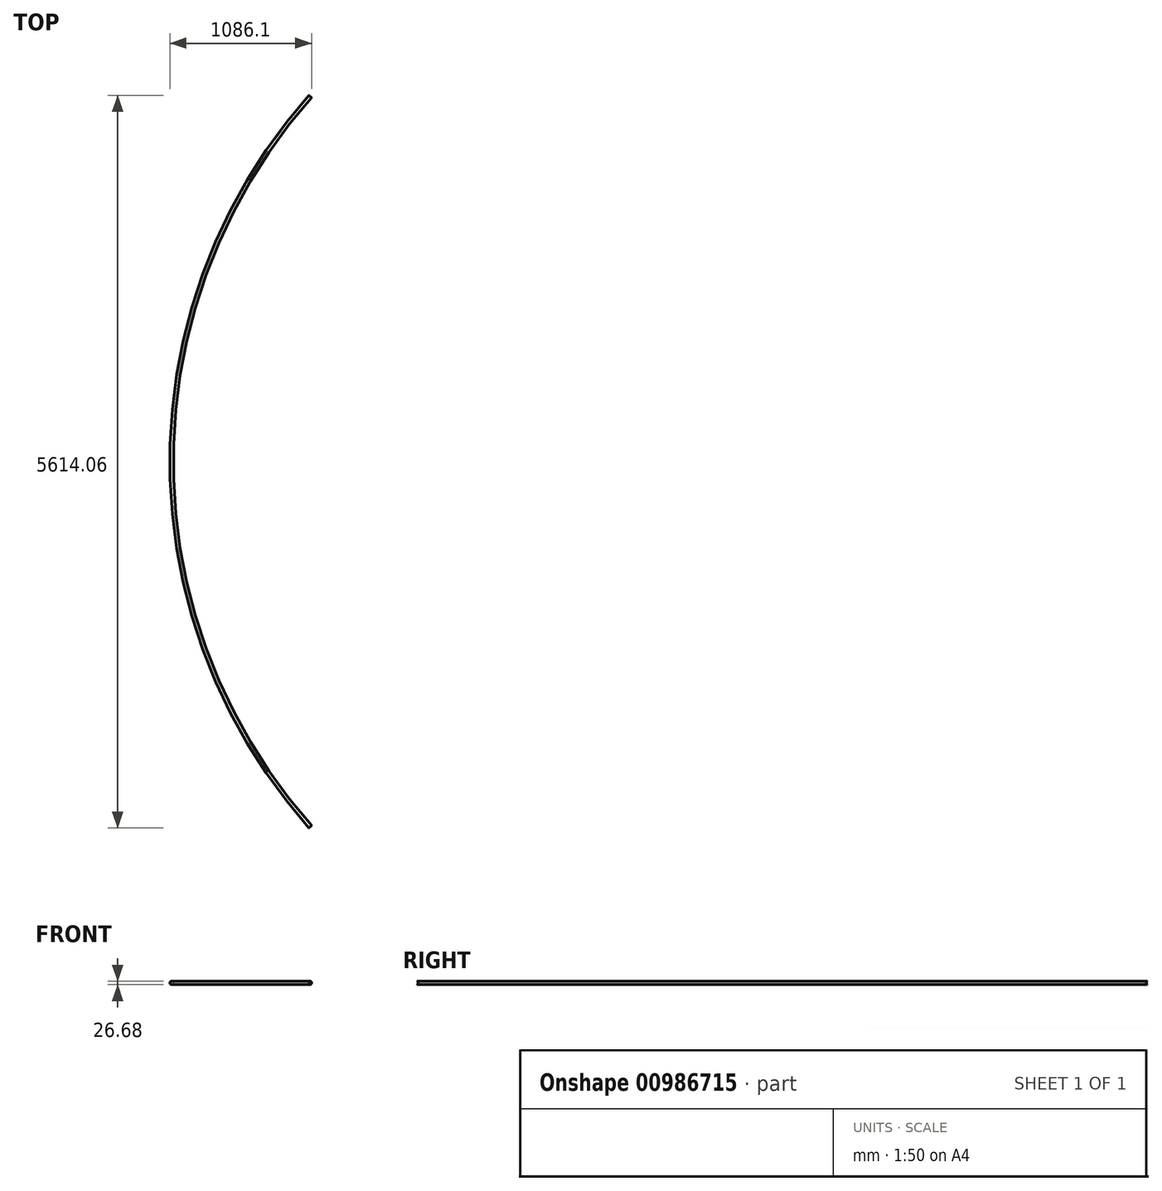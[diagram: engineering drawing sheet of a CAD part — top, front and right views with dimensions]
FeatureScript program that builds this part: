
annotation { "Feature Type Name" : "Feature", "Feature Type Description" : "" }
export const myFeature = defineFeature(function(context is Context, id is Id, definition is map)
    precondition{}
    {
        {
            var Q0;
            Q0=qCreatedBy(makeId("Front.planeOp"),FACE);
            var sketch = newSketch(context, id + "F0", { "sketchPlane" : qUnion([Q0])});
            skLineSegment(sketch, "E0", {"start": v(0, 0) * mm, "end": v(-4215, 0) * mm, "construction": true});
            skCircle(sketch, "E1", {"center": v(-4215, 0) * mm, "radius": 13.33 * mm});
            skCircle(sketch, "E2.0", {"center": v(-4215, 0) * mm, "radius": 11.23 * mm});
            skLineSegment(sketch, "E3", {"start": v(0, 0) * mm, "end": v(0, -25) * mm, "construction": true});
            skSolve(sketch);
        }
        {
            var Q0;
            Q0=makeQuery(id+"F0.imprint","IMPRINT",FACE,{"disambiguationData":[TD([[makeQuery(id+"F0.imprint","IMPRINT",EDGE,{"derivedFrom":sQuery(id+"F0.wireOp",EDGE,"E1")}),1.0]])]});
            var Q1;
            Q1=sQuery(id+"F0.wireOp",EDGE,"E3");
            revolve(context, id + "F1", {"surfaceOperationType" : NewSurfaceOperationType.NEW, "entities" : qUnion([Q0]), "axis" : qUnion([Q1]), "revolveType" : RevolveType.SYMMETRIC, "angle" : 83.19 * degree});
        }
    });
